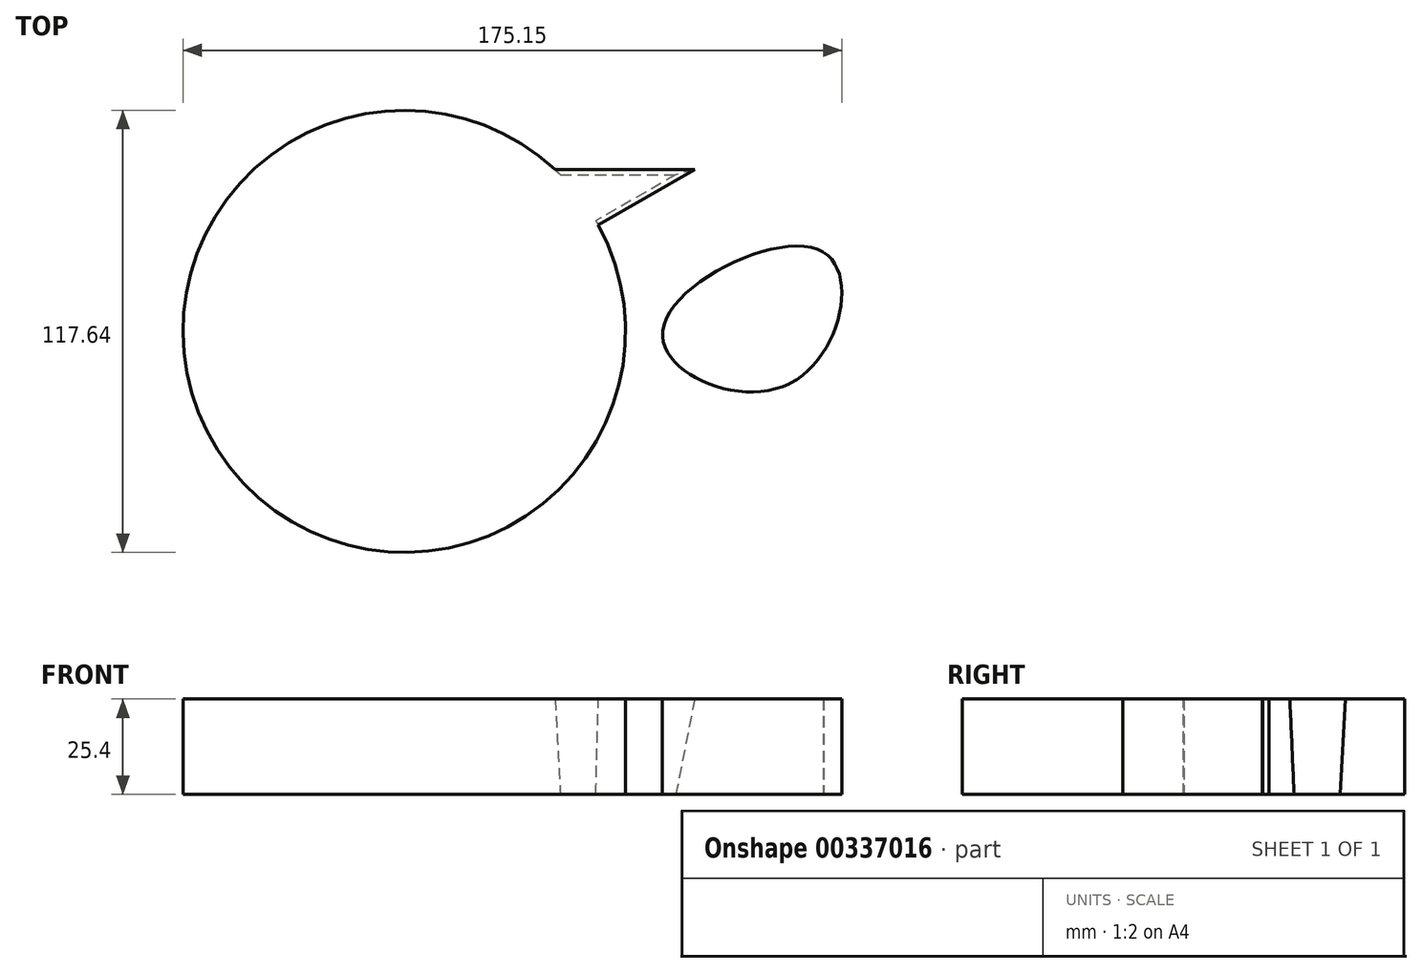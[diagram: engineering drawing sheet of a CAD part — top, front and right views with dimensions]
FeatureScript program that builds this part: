
annotation { "Feature Type Name" : "Feature", "Feature Type Description" : "" }
export const myFeature = defineFeature(function(context is Context, id is Id, definition is map)
    precondition{}
    {
        {
            var Q0;
            Q0=qCreatedBy(makeId("Top.planeOp"),FACE);
            var sketch = newSketch(context, id + "F0", { "sketchPlane" : qUnion([Q0])});
            skLineSegment(sketch, "E0", {"start": v(21.78, 41.7) * mm, "end": v(0, 0) * mm});
            skLineSegment(sketch, "E1", {"start": v(0, 0) * mm, "end": v(72.2, 41.7) * mm});
            skLineSegment(sketch, "E2", {"start": v(72.2, 41.7) * mm, "end": v(21.78, 41.7) * mm});
            skSolve(sketch);
        }
        {
            var Q0;
            Q0 = qSketchRegion(id + "F0", true);
            extrude(context, id + "F1", {"entities" : qUnion([Q0]), "depth" : 25.4 * mm, "hasDraft" : true, "draftAngle" : 3 * degree});
        }
        {
            var Q0;
            Q0=qCreatedBy(makeId("Top.planeOp"),FACE);
            var sketch = newSketch(context, id + "F2", { "sketchPlane" : qUnion([Q0])});
            skCircle(sketch, "E3", {"center": v(0, 0) * mm, "radius": 58.82 * mm});
            skSolve(sketch);
        }
        {
            var Q0;
            Q0 = qSketchRegion(id + "F2", true);
            extrude(context, id + "F3", {"entities" : qUnion([Q0]), "operationType" : NewBodyOperationType.ADD, "depth" : 25.4 * mm});
        }
        {
            var Q0;
            Q0=qCreatedBy(makeId("Top.planeOp"),FACE);
            var sketch = newSketch(context, id + "F4", { "sketchPlane" : qUnion([Q0])});
            skFitSpline(sketch, "E4", {"points": [v(68.67, 0) * mm, v(102.35, -13.93) * mm, v(111.5, 21) * mm, v(68.67, 0) * mm]});
            skFitSpline(sketch, "E5", {"points": [v(92.58, 0) * mm, v(111.5, 21) * mm, v(102.35, -13.93) * mm, v(68.67, 0) * mm, v(92.58, 0) * mm]});
            skSolve(sketch);
        }
        {
            var Q0;
            Q0 = qSketchRegion(id + "F4", true);
            extrude(context, id + "F5", {"entities" : qUnion([Q0]), "depth" : 25.4 * mm});
        }
    });
